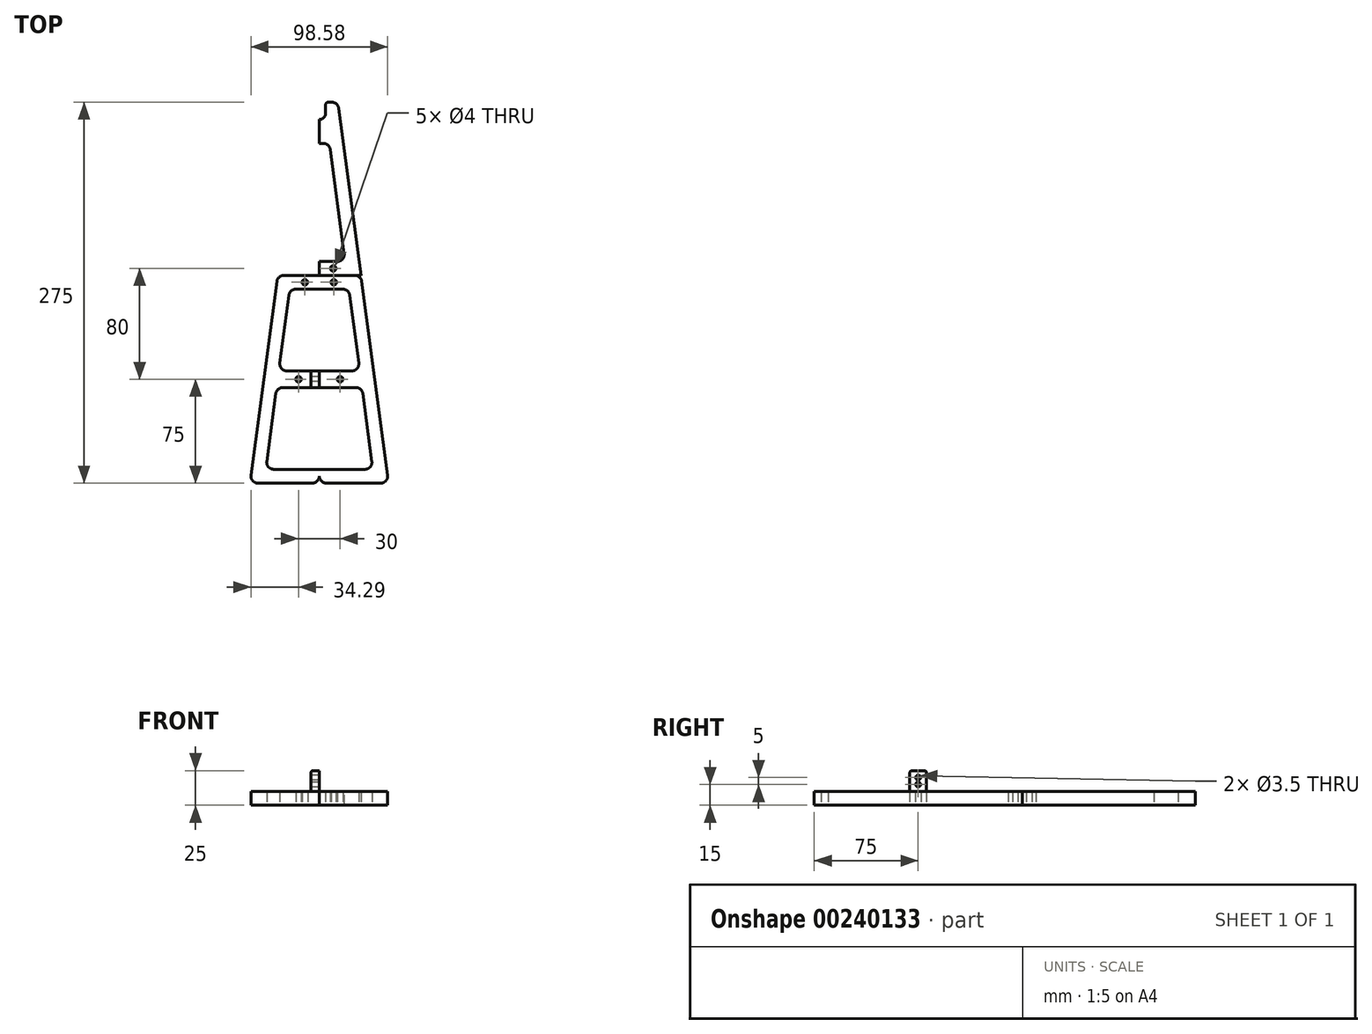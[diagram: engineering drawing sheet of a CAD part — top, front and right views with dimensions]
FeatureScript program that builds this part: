
annotation { "Feature Type Name" : "Feature", "Feature Type Description" : "" }
export const myFeature = defineFeature(function(context is Context, id is Id, definition is map)
    precondition{}
    {
        {
            var Q0;
            Q0=qCreatedBy(makeId("Top.planeOp"),FACE);
            var sketch = newSketch(context, id + "F0", { "sketchPlane" : qUnion([Q0])});
            skLineSegment(sketch, "E0.top", {"start": v(0, 75) * mm, "end": v(-30, 75) * mm});
            skPoint(sketch, "E0.middle", {"position": v(0, 0) * mm});
            skLineSegment(sketch, "E1", {"start": v(-30, 75) * mm, "end": v(-50, -75) * mm});
            skPoint(sketch, "E0.right.end.orphan", {"position": v(-50, 75) * mm});
            skPoint(sketch, "E0.left.end.orphan", {"position": v(50, 75) * mm});
            skLineSegment(sketch, "E2", {"start": v(0, 0) * mm, "end": v(0, 6) * mm});
            skLineSegment(sketch, "E3", {"start": v(-50, -75) * mm, "end": v(-40, -75) * mm});
            skLineSegment(sketch, "E4", {"start": v(-30, 75) * mm, "end": v(-20, 75) * mm});
            skLineSegment(sketch, "E5", {"start": v(0, 75) * mm, "end": v(0, 65) * mm});
            skLineSegment(sketch, "E6", {"start": v(0, 65) * mm, "end": v(-21.33, 65) * mm});
            skLineSegment(sketch, "E7", {"start": v(0, -75) * mm, "end": v(0, -65) * mm});
            skLineSegment(sketch, "E8", {"start": v(0, -65) * mm, "end": v(-38.67, -65) * mm});
            skLineSegment(sketch, "E9", {"start": v(0, 6) * mm, "end": v(-29.2, 6) * mm});
            skLineSegment(sketch, "E10", {"start": v(0, 0) * mm, "end": v(0, -6) * mm});
            skLineSegment(sketch, "E11", {"start": v(0, -6) * mm, "end": v(-30.8, -6) * mm});
            skLineSegment(sketch, "E12.trimOffspring", {"start": v(-30.8, -6) * mm, "end": v(-38.67, -65) * mm});
            skLineSegment(sketch, "E13", {"start": v(-21.33, 65) * mm, "end": v(-29.2, 6) * mm});
            skLineSegment(sketch, "E14.trimOffspring", {"start": v(0, -75) * mm, "end": v(-50, -75) * mm});
            skPoint(sketch, "E0.bottom.start.orphan", {"position": v(50, -75) * mm});
            skCircle(sketch, "E15", {"center": v(-15, 0) * mm, "radius": 2 * mm});
            skLineSegment(sketch, "E16", {"start": v(0, 65) * mm, "end": v(0, 70) * mm});
            skCircle(sketch, "E17", {"center": v(-10.41, 70) * mm, "radius": 2 * mm});
            skSolve(sketch);
        }
        {
            var Q0;
            Q0=qSketchRegion(id+"F0",true);
            extrude(context, id + "F1", {"entities" : qUnion([Q0]), "depth" : 10 * mm});
        }
        {
            var Q0;
            Q0=makeQuery(id+"F1.opExtrude","SWEPT_EDGE",EDGE,{"disambiguationData":[OSD([sQuery(id+"F0.wireOp",EDGE,"E6"),sQuery(id+"F0.wireOp",EDGE,"E13")])]});
            var Q1;
            Q1=makeQuery(id+"F1.opExtrude","SWEPT_EDGE",EDGE,{"disambiguationData":[OSD([sQuery(id+"F0.wireOp",EDGE,"E11"),sQuery(id+"F0.wireOp",EDGE,"E12.trimOffspring")])]});
            var Q2;
            Q2=makeQuery(id+"F1.opExtrude","SWEPT_EDGE",EDGE,{"disambiguationData":[OSD([sQuery(id+"F0.wireOp",EDGE,"E9"),sQuery(id+"F0.wireOp",EDGE,"E13")])]});
            var Q3;
            Q3=makeQuery(id+"F1.opExtrude","SWEPT_EDGE",EDGE,{"disambiguationData":[OSD([sQuery(id+"F0.wireOp",EDGE,"E8"),sQuery(id+"F0.wireOp",EDGE,"E12.trimOffspring")])]});
            var Q4;
            Q4=makeQuery(id+"F1.opExtrude","SWEPT_EDGE",EDGE,{"disambiguationData":[OSD([sQuery(id+"F0.wireOp",EDGE,"E1"),sQuery(id+"F0.wireOp",EDGE,"E14.trimOffspring")])]});
            fillet(context, id + "F2", {"entities" : qUnion([Q0, Q1, Q2, Q3, Q4]), "radius" : 5 * mm, "tangentPropagation" : true, "allowEdgeOverflow" : false});
        }
        {
            var Q0;
            Q0=makeQuery(id+"F1.opExtrude","SWEPT_BODY",BODY,{"disambiguationData":[OSD([sQuery(id+"F0.wireOp",EDGE,"E0.top"),sQuery(id+"F0.wireOp",EDGE,"E1"),sQuery(id+"F0.wireOp",EDGE,"E2"),sQuery(id+"F0.wireOp",EDGE,"E4"),sQuery(id+"F0.wireOp",EDGE,"E5"),sQuery(id+"F0.wireOp",EDGE,"E6"),sQuery(id+"F0.wireOp",EDGE,"E7"),sQuery(id+"F0.wireOp",EDGE,"E8"),sQuery(id+"F0.wireOp",EDGE,"E9"),sQuery(id+"F0.wireOp",EDGE,"E10"),sQuery(id+"F0.wireOp",EDGE,"E11"),sQuery(id+"F0.wireOp",EDGE,"E12.trimOffspring"),sQuery(id+"F0.wireOp",EDGE,"E13"),sQuery(id+"F0.wireOp",EDGE,"E14.trimOffspring"),sQuery(id+"F0.wireOp",EDGE,"E15"),sQuery(id+"F0.wireOp",EDGE,"E16"),sQuery(id+"F0.wireOp",EDGE,"E17")])]});
            var Q1;
            Q1=qCreatedBy(makeId("Right.planeOp"),FACE);
            mirror(context, id + "F3", {"operationType" : NewBodyOperationType.ADD, "entities" : qUnion([Q0]), "mirrorPlane" : qUnion([Q1])});
        }
        {
            var Q0;
            Q0=qCreatedBy(makeId("Top.planeOp"),FACE);
            var sketch = newSketch(context, id + "F4", { "sketchPlane" : qUnion([Q0])});
            skLineSegment(sketch, "E18", {"start": v(0, 0) * mm, "end": v(40, 0) * mm});
            skLineSegment(sketch, "E19", {"start": v(0, 75) * mm, "end": v(30, 75) * mm});
            skLineSegment(sketch, "E20", {"start": v(0, 75) * mm, "end": v(0, 85) * mm});
            skLineSegment(sketch, "E21", {"start": v(4.5, 200) * mm, "end": v(13.33, 200) * mm});
            skLineSegment(sketch, "E22", {"start": v(30, 75) * mm, "end": v(13.33, 200) * mm});
            skArc(sketch, "E23", {"start": v(0, 187.5) * mm, "mid": v(3.18, 188.82) * mm, "end": v(4.5, 192) * mm});
            skLineSegment(sketch, "E24", {"start": v(4.5, 200) * mm, "end": v(4.5, 192) * mm});
            skLineSegment(sketch, "E25", {"start": v(0, 75) * mm, "end": v(0, 80) * mm});
            skCircle(sketch, "E26", {"center": v(10, 80) * mm, "radius": 2 * mm});
            skLineSegment(sketch, "E27", {"start": v(0, 75) * mm, "end": v(10, 75) * mm});
            skLineSegment(sketch, "E28", {"start": v(10, 85) * mm, "end": v(18.67, 85) * mm});
            skLineSegment(sketch, "E29", {"start": v(18.67, 85) * mm, "end": v(10, 150) * mm});
            skLineSegment(sketch, "E30", {"start": v(10, 85) * mm, "end": v(0, 85) * mm});
            skLineSegment(sketch, "E31", {"start": v(18.67, 85) * mm, "end": v(7.31, 170.17) * mm});
            skLineSegment(sketch, "E32", {"start": v(7.31, 170.17) * mm, "end": v(0, 170.17) * mm});
            skLineSegment(sketch, "E33.trimOffspring", {"start": v(0, 170.17) * mm, "end": v(0, 187.5) * mm});
            skSolve(sketch);
        }
        {
            var Q0;
            Q0 = qSketchRegion(id + "F4", true);
            extrude(context, id + "F5", {"entities" : qUnion([Q0]), "depth" : 10 * mm});
        }
        {
            var Q0;
            Q0=makeQuery(id+"F5.opExtrude","SWEPT_BODY",BODY,{"disambiguationData":[OSD([sQuery(id+"F4.wireOp",EDGE,"E19"),sQuery(id+"F4.wireOp",EDGE,"E20"),sQuery(id+"F4.wireOp",EDGE,"E21"),sQuery(id+"F4.wireOp",EDGE,"E22"),sQuery(id+"F4.wireOp",EDGE,"E23"),sQuery(id+"F4.wireOp",EDGE,"E24"),sQuery(id+"F4.wireOp",EDGE,"E25"),sQuery(id+"F4.wireOp",EDGE,"E26"),sQuery(id+"F4.wireOp",EDGE,"E27"),sQuery(id+"F4.wireOp",EDGE,"E28"),sQuery(id+"F4.wireOp",EDGE,"E30"),sQuery(id+"F4.wireOp",EDGE,"E31"),sQuery(id+"F4.wireOp",EDGE,"E32"),sQuery(id+"F4.wireOp",EDGE,"E33.trimOffspring")])]});
            var Q1;
            Q1=qCreatedBy(makeId("Right.planeOp"),FACE);
            mirror(context, id + "F6", {"entities" : qUnion([Q0]), "mirrorPlane" : qUnion([Q1])});
        }
        {
            var Q0;
            Q0=makeQuery(id+"F6.opPattern","COPY",EDGE,{"derivedFrom":makeQuery(id+"F5.opExtrude","SWEPT_EDGE",EDGE,{"disambiguationData":[OSD([sQuery(id+"F4.wireOp",EDGE,"E31"),sQuery(id+"F4.wireOp",EDGE,"E32")])]}),"instanceName":"1"});
            var Q1;
            Q1=makeQuery(id+"F5.opExtrude","SWEPT_EDGE",EDGE,{"disambiguationData":[OSD([sQuery(id+"F4.wireOp",EDGE,"E31"),sQuery(id+"F4.wireOp",EDGE,"E32")])]});
            var Q2;
            Q2=makeQuery(id+"F6.opPattern","COPY",EDGE,{"derivedFrom":makeQuery(id+"F5.opExtrude","SWEPT_EDGE",EDGE,{"disambiguationData":[OSD([sQuery(id+"F4.wireOp",EDGE,"E28"),sQuery(id+"F4.wireOp",EDGE,"E31")])]}),"instanceName":"1"});
            var Q3;
            Q3=makeQuery(id+"F5.opExtrude","SWEPT_EDGE",EDGE,{"disambiguationData":[OSD([sQuery(id+"F4.wireOp",EDGE,"E28"),sQuery(id+"F4.wireOp",EDGE,"E31")])]});
            var Q4;
            Q4=makeQuery(id+"F6.opPattern","COPY",EDGE,{"derivedFrom":makeQuery(id+"F5.opExtrude","SWEPT_EDGE",EDGE,{"disambiguationData":[OSD([sQuery(id+"F4.wireOp",EDGE,"E21"),sQuery(id+"F4.wireOp",EDGE,"E22")])]}),"instanceName":"1"});
            var Q5;
            Q5=makeQuery(id+"F5.opExtrude","SWEPT_EDGE",EDGE,{"disambiguationData":[OSD([sQuery(id+"F4.wireOp",EDGE,"E21"),sQuery(id+"F4.wireOp",EDGE,"E22")])]});
            fillet(context, id + "F7", {"entities" : qUnion([Q0, Q1, Q2, Q3, Q4, Q5]), "radius" : 5 * mm, "tangentPropagation" : true, "allowEdgeOverflow" : false});
        }
        {
            var Q0;
            Q0=makeQuery(id+"F5.opExtrude","SWEPT_EDGE",EDGE,{"disambiguationData":[OSD([sQuery(id+"F4.wireOp",EDGE,"E21"),sQuery(id+"F4.wireOp",EDGE,"E24")])]});
            var Q1;
            Q1=makeQuery(id+"F6.opPattern","COPY",EDGE,{"derivedFrom":makeQuery(id+"F5.opExtrude","SWEPT_EDGE",EDGE,{"disambiguationData":[OSD([sQuery(id+"F4.wireOp",EDGE,"E21"),sQuery(id+"F4.wireOp",EDGE,"E24")])]}),"instanceName":"1"});
            fillet(context, id + "F8", {"entities" : qUnion([Q0, Q1]), "radius" : 2 * mm, "tangentPropagation" : true, "allowEdgeOverflow" : false});
        }
        {
            var Q0;
            Q0=qCreatedBy(makeId("Top.planeOp"),FACE);
            var sketch = newSketch(context, id + "F9", { "sketchPlane" : qUnion([Q0])});
            skLineSegment(sketch, "E34", {"start": v(0, 0) * mm, "end": v(0, 6) * mm});
            skLineSegment(sketch, "E35", {"start": v(0, 6) * mm, "end": v(-6, 6) * mm});
            skLineSegment(sketch, "E36", {"start": v(-6, 6) * mm, "end": v(-6, -6) * mm});
            skLineSegment(sketch, "E37", {"start": v(-6, -6) * mm, "end": v(0, -6) * mm});
            skLineSegment(sketch, "E38", {"start": v(0, -6) * mm, "end": v(0, 0) * mm});
            skSolve(sketch);
        }
        {
            var Q0;
            Q0 = qSketchRegion(id + "F9", true);
            extrude(context, id + "F10", {"entities" : qUnion([Q0]), "operationType" : NewBodyOperationType.ADD, "depth" : 25 * mm});
        }
        {
            var Q0;
            Q0=makeQuery(id+"F10.opExtrude","SWEPT_EDGE",EDGE,{"disambiguationData":[OSD([sQuery(id+"F9.wireOp",EDGE,"E36"),sQuery(id+"F9.wireOp",EDGE,"E37")])]});
            var Q1;
            Q1=makeQuery(id+"F10.opExtrude","CAP_EDGE",EDGE,{"disambiguationData":[OSD([sQuery(id+"F9.wireOp",EDGE,"E36")])],"isStart":false});
            var Q2;
            Q2=makeQuery(id+"F10.opExtrude","CAP_EDGE",EDGE,{"disambiguationData":[OSD([sQuery(id+"F9.wireOp",EDGE,"E37")])],"isStart":false});
            var Q3;
            Q3=makeQuery(id+"F10.opExtrude","SWEPT_EDGE",EDGE,{"disambiguationData":[OSD([sQuery(id+"F9.wireOp",EDGE,"E35"),sQuery(id+"F9.wireOp",EDGE,"E36")])]});
            var Q4;
            Q4=makeQuery(id+"F10.opExtrude","CAP_EDGE",EDGE,{"disambiguationData":[OSD([sQuery(id+"F9.wireOp",EDGE,"E35")])],"isStart":false});
            fillet(context, id + "F11", {"entities" : qUnion([Q0, Q1, Q2, Q3, Q4]), "radius" : 1.5 * mm, "tangentPropagation" : true, "allowEdgeOverflow" : false});
        }
        {
            var Q0;
            Q0=qCreatedBy(makeId("Right.planeOp"),FACE);
            var sketch = newSketch(context, id + "F12", { "sketchPlane" : qUnion([Q0])});
            skCircle(sketch, "E39", {"center": v(0, 20) * mm, "radius": 1.75 * mm});
            skCircle(sketch, "E40", {"center": v(0, 15) * mm, "radius": 1.75 * mm});
            skSolve(sketch);
        }
        {
            var Q0;
            Q0 = qSketchRegion(id + "F12", true);
            extrude(context, id + "F13", {"entities" : qUnion([Q0]), "endBound" : BoundingType.SYMMETRIC, "depth" : 25 * mm});
        }
        {
            var Q0;
            Q0=makeQuery(id+"F13.opExtrude","SWEPT_BODY",BODY,{"disambiguationData":[OSD([sQuery(id+"F12.wireOp",EDGE,"E40")])]});
            var Q1;
            Q1=makeQuery(id+"F13.opExtrude","SWEPT_BODY",BODY,{"disambiguationData":[OSD([sQuery(id+"F12.wireOp",EDGE,"E39")])]});
            var Q2;
            Q2=makeQuery(id+"F1.opExtrude","SWEPT_BODY",BODY,{"disambiguationData":[OSD([sQuery(id+"F0.wireOp",EDGE,"E0.top"),sQuery(id+"F0.wireOp",EDGE,"E1"),sQuery(id+"F0.wireOp",EDGE,"E2"),sQuery(id+"F0.wireOp",EDGE,"E4"),sQuery(id+"F0.wireOp",EDGE,"E5"),sQuery(id+"F0.wireOp",EDGE,"E6"),sQuery(id+"F0.wireOp",EDGE,"E7"),sQuery(id+"F0.wireOp",EDGE,"E8"),sQuery(id+"F0.wireOp",EDGE,"E9"),sQuery(id+"F0.wireOp",EDGE,"E10"),sQuery(id+"F0.wireOp",EDGE,"E11"),sQuery(id+"F0.wireOp",EDGE,"E12.trimOffspring"),sQuery(id+"F0.wireOp",EDGE,"E13"),sQuery(id+"F0.wireOp",EDGE,"E14.trimOffspring"),sQuery(id+"F0.wireOp",EDGE,"E15"),sQuery(id+"F0.wireOp",EDGE,"E16"),sQuery(id+"F0.wireOp",EDGE,"E17")])]});
            booleanBodies(context, id + "F14", {"operationType" : BooleanOperationType.SUBTRACTION, "tools" : qUnion([Q0, Q1]), "targets" : qUnion([Q2])});
        }
        {
            var Q0;
            Q0=qCreatedBy(makeId("Top.planeOp"),FACE);
            var sketch = newSketch(context, id + "F15", { "sketchPlane" : qUnion([Q0])});
            skLineSegment(sketch, "E41.bottom", {"start": v(15, 65) * mm, "end": v(-15, 65) * mm});
            skLineSegment(sketch, "E41.top", {"start": v(15, 85) * mm, "end": v(-15, 85) * mm});
            skLineSegment(sketch, "E41.left", {"start": v(15, 65) * mm, "end": v(15, 85) * mm});
            skLineSegment(sketch, "E41.right", {"start": v(-15, 65) * mm, "end": v(-15, 85) * mm});
            skPoint(sketch, "E41.middle", {"position": v(0, 75) * mm});
            skLineSegment(sketch, "E42", {"start": v(0, 75) * mm, "end": v(0, 85) * mm});
            skLineSegment(sketch, "E43", {"start": v(0, 85) * mm, "end": v(0, 65) * mm});
            skLineSegment(sketch, "E44", {"start": v(0, 65) * mm, "end": v(-6, 65) * mm});
            skLineSegment(sketch, "E45", {"start": v(-6, 65) * mm, "end": v(-6, 85) * mm});
            skLineSegment(sketch, "E46", {"start": v(-6, 85) * mm, "end": v(0, 85) * mm});
            skSolve(sketch);
        }
        {
            var Q0;
            Q0 = qSketchRegion(id + "F15", true);
            extrude(context, id + "F16", {"entities" : qUnion([Q0]), "depth" : 10 * mm});
        }
        {
            var Q0;
            Q0=qCreatedBy(makeId("Top.planeOp"),FACE);
            var sketch = newSketch(context, id + "F17", { "sketchPlane" : qUnion([Q0])});
            skLineSegment(sketch, "E47", {"start": v(0, 65) * mm, "end": v(0, 85) * mm});
            skLineSegment(sketch, "E48", {"start": v(0, 85) * mm, "end": v(-6, 85) * mm});
            skLineSegment(sketch, "E49", {"start": v(-6, 85) * mm, "end": v(-6, 65) * mm});
            skLineSegment(sketch, "E50", {"start": v(-6, 65) * mm, "end": v(0, 65) * mm});
            skSolve(sketch);
        }
        {
            var Q0;
            Q0 = qSketchRegion(id + "F17", true);
            extrude(context, id + "F18", {"entities" : qUnion([Q0]), "depth" : 25 * mm});
        }
        {
            var Q0;
            Q0=makeQuery(id+"F16.opExtrude","SWEPT_BODY",BODY,{"disambiguationData":[OSD([sQuery(id+"F15.wireOp",EDGE,"E41.bottom"),sQuery(id+"F15.wireOp",EDGE,"E41.top"),sQuery(id+"F15.wireOp",EDGE,"E41.left"),sQuery(id+"F15.wireOp",EDGE,"E41.right"),sQuery(id+"F15.wireOp",EDGE,"E44"),sQuery(id+"F15.wireOp",EDGE,"E46")])]});
            var Q1;
            Q1=makeQuery(id+"F18.opExtrude","SWEPT_BODY",BODY,{"disambiguationData":[OSD([sQuery(id+"F17.wireOp",EDGE,"E47"),sQuery(id+"F17.wireOp",EDGE,"E48"),sQuery(id+"F17.wireOp",EDGE,"E49"),sQuery(id+"F17.wireOp",EDGE,"E50")])]});
            booleanBodies(context, id + "F19", {"operationType" : BooleanOperationType.UNION, "tools" : qUnion([Q0, Q1])});
        }
        {
            var Q0;
            Q0=makeQuery(id+"F16.opExtrude","SWEPT_BODY",BODY,{"disambiguationData":[OSD([sQuery(id+"F15.wireOp",EDGE,"E41.bottom"),sQuery(id+"F15.wireOp",EDGE,"E41.top"),sQuery(id+"F15.wireOp",EDGE,"E41.left"),sQuery(id+"F15.wireOp",EDGE,"E41.right"),sQuery(id+"F15.wireOp",EDGE,"E44"),sQuery(id+"F15.wireOp",EDGE,"E46")])]});
            transform(context, id + "F20", {"entities" : qUnion([Q0]), "transformType" : TransformType.TRANSLATION_3D, "dx" : 0 * mm, "dy" : 0 * mm, "dz" : 10 * mm, "makeCopy" : false});
        }
        {
            var Q0;
            Q0=qCreatedBy(makeId("Top.planeOp"),FACE);
            var sketch = newSketch(context, id + "F21", { "sketchPlane" : qUnion([Q0])});
            skCircle(sketch, "E51", {"center": v(-10, 80) * mm, "radius": 2 * mm});
            skCircle(sketch, "E52", {"center": v(10, 80) * mm, "radius": 2 * mm});
            skCircle(sketch, "E53", {"center": v(-10.4, 70) * mm, "radius": 2 * mm});
            skCircle(sketch, "E54", {"center": v(10.4, 70) * mm, "radius": 2 * mm});
            skSolve(sketch);
        }
        {
            var Q0;
            Q0 = qSketchRegion(id + "F21", true);
            extrude(context, id + "F22", {"entities" : qUnion([Q0]), "depth" : 30 * mm});
        }
        {
            var Q0;
            Q0=makeQuery(id+"F22.opExtrude","SWEPT_BODY",BODY,{"disambiguationData":[OSD([sQuery(id+"F21.wireOp",EDGE,"E54")])]});
            var Q1;
            Q1=makeQuery(id+"F22.opExtrude","SWEPT_BODY",BODY,{"disambiguationData":[OSD([sQuery(id+"F21.wireOp",EDGE,"E53")])]});
            var Q2;
            Q2=makeQuery(id+"F22.opExtrude","SWEPT_BODY",BODY,{"disambiguationData":[OSD([sQuery(id+"F21.wireOp",EDGE,"E52")])]});
            var Q3;
            Q3=makeQuery(id+"F22.opExtrude","SWEPT_BODY",BODY,{"disambiguationData":[OSD([sQuery(id+"F21.wireOp",EDGE,"E51")])]});
            var Q4;
            Q4=makeQuery(id+"F16.opExtrude","SWEPT_BODY",BODY,{"disambiguationData":[OSD([sQuery(id+"F15.wireOp",EDGE,"E41.bottom"),sQuery(id+"F15.wireOp",EDGE,"E41.top"),sQuery(id+"F15.wireOp",EDGE,"E41.left"),sQuery(id+"F15.wireOp",EDGE,"E41.right"),sQuery(id+"F15.wireOp",EDGE,"E44"),sQuery(id+"F15.wireOp",EDGE,"E46")])]});
            booleanBodies(context, id + "F23", {"operationType" : BooleanOperationType.SUBTRACTION, "tools" : qUnion([Q0, Q1, Q2, Q3]), "targets" : qUnion([Q4])});
        }
        {
            var Q0;
            Q0=qCreatedBy(makeId("Right.planeOp"),FACE);
            var sketch = newSketch(context, id + "F24", { "sketchPlane" : qUnion([Q0])});
            skCircle(sketch, "E55", {"center": v(80, 27.23) * mm, "radius": 2 * mm});
            skCircle(sketch, "E56", {"center": v(70, 27.23) * mm, "radius": 2 * mm});
            skSolve(sketch);
        }
        {
            var Q0;
            Q0 = qSketchRegion(id + "F24", true);
            extrude(context, id + "F25", {"entities" : qUnion([Q0]), "endBound" : BoundingType.SYMMETRIC, "depth" : 25 * mm});
        }
        {
            var Q0;
            Q0=makeQuery(id+"F25.opExtrude","SWEPT_BODY",BODY,{"disambiguationData":[OSD([sQuery(id+"F24.wireOp",EDGE,"E56")])]});
            var Q1;
            Q1=makeQuery(id+"F25.opExtrude","SWEPT_BODY",BODY,{"disambiguationData":[OSD([sQuery(id+"F24.wireOp",EDGE,"E55")])]});
            var Q2;
            Q2=makeQuery(id+"F16.opExtrude","SWEPT_BODY",BODY,{"disambiguationData":[OSD([sQuery(id+"F15.wireOp",EDGE,"E41.bottom"),sQuery(id+"F15.wireOp",EDGE,"E41.top"),sQuery(id+"F15.wireOp",EDGE,"E41.left"),sQuery(id+"F15.wireOp",EDGE,"E41.right"),sQuery(id+"F15.wireOp",EDGE,"E44"),sQuery(id+"F15.wireOp",EDGE,"E46")])]});
            booleanBodies(context, id + "F26", {"operationType" : BooleanOperationType.SUBTRACTION, "tools" : qUnion([Q0, Q1]), "targets" : qUnion([Q2])});
        }
        {
            var Q0;
            Q0=makeQuery(id+"F18.opExtrude","SWEPT_EDGE",EDGE,{"disambiguationData":[OSD([sQuery(id+"F17.wireOp",EDGE,"E49"),sQuery(id+"F17.wireOp",EDGE,"E50")])]});
            var Q1;
            Q1=makeQuery(id+"F18.opExtrude","CAP_EDGE",EDGE,{"disambiguationData":[OSD([sQuery(id+"F17.wireOp",EDGE,"E50")])],"isStart":false});
            var Q2;
            {var subQ0=sQuery(id+"F15.wireOp",EDGE,"E44");var subQ1=sQuery(id+"F15.wireOp",EDGE,"E41.bottom");var subQ2=sQuery(id+"F15.wireOp",EDGE,"E41.right");Q2=makeQuery(id+"F19.opBoolean","SPLIT",EDGE,{"disambiguationData":[TD([makeQuery(id+"F16.opExtrude","SWEPT_FACE",FACE,{"disambiguationData":[OSD([subQ2])]})])],"derivedFrom":makeQuery(id+"F16.opExtrude","CAP_EDGE",EDGE,{"disambiguationData":[OSD([subQ1,subQ0])],"isStart":false})});}
            var Q3;
            Q3=makeQuery(id+"F16.opExtrude","SWEPT_EDGE",EDGE,{"disambiguationData":[OSD([sQuery(id+"F15.wireOp",EDGE,"E41.bottom"),sQuery(id+"F15.wireOp",EDGE,"E41.right")])]});
            var Q4;
            {var subQ0=sQuery(id+"F15.wireOp",EDGE,"E41.left");var subQ1=sQuery(id+"F15.wireOp",EDGE,"E44");var subQ2=sQuery(id+"F15.wireOp",EDGE,"E41.bottom");Q4=makeQuery(id+"F19.opBoolean","SPLIT",EDGE,{"disambiguationData":[TD([makeQuery(id+"F16.opExtrude","SWEPT_FACE",FACE,{"disambiguationData":[OSD([subQ0])]})])],"derivedFrom":makeQuery(id+"F16.opExtrude","CAP_EDGE",EDGE,{"disambiguationData":[OSD([subQ2,subQ1])],"isStart":false})});}
            var Q5;
            Q5=makeQuery(id+"F16.opExtrude","SWEPT_EDGE",EDGE,{"disambiguationData":[OSD([sQuery(id+"F15.wireOp",EDGE,"E41.bottom"),sQuery(id+"F15.wireOp",EDGE,"E41.left")])]});
            var Q6;
            Q6=makeQuery(id+"F16.opExtrude","CAP_EDGE",EDGE,{"disambiguationData":[OSD([sQuery(id+"F15.wireOp",EDGE,"E41.left")])],"isStart":false});
            var Q7;
            Q7=makeQuery(id+"F16.opExtrude","CAP_EDGE",EDGE,{"disambiguationData":[OSD([sQuery(id+"F15.wireOp",EDGE,"E41.right")])],"isStart":false});
            var Q8;
            Q8=makeQuery(id+"F18.opExtrude","CAP_EDGE",EDGE,{"disambiguationData":[OSD([sQuery(id+"F17.wireOp",EDGE,"E49")])],"isStart":false});
            var Q9;
            {var subQ0=sQuery(id+"F15.wireOp",EDGE,"E41.right");var subQ1=sQuery(id+"F15.wireOp",EDGE,"E46");var subQ2=sQuery(id+"F15.wireOp",EDGE,"E41.top");Q9=makeQuery(id+"F19.opBoolean","SPLIT",EDGE,{"disambiguationData":[TD([makeQuery(id+"F16.opExtrude","SWEPT_FACE",FACE,{"disambiguationData":[OSD([subQ0])]})])],"derivedFrom":makeQuery(id+"F16.opExtrude","CAP_EDGE",EDGE,{"disambiguationData":[OSD([subQ2,subQ1])],"isStart":false})});}
            var Q10;
            Q10=makeQuery(id+"F16.opExtrude","SWEPT_EDGE",EDGE,{"disambiguationData":[OSD([sQuery(id+"F15.wireOp",EDGE,"E41.top"),sQuery(id+"F15.wireOp",EDGE,"E41.right")])]});
            var Q11;
            Q11=makeQuery(id+"F18.opExtrude","SWEPT_EDGE",EDGE,{"disambiguationData":[OSD([sQuery(id+"F17.wireOp",EDGE,"E48"),sQuery(id+"F17.wireOp",EDGE,"E49")])]});
            var Q12;
            Q12=makeQuery(id+"F18.opExtrude","CAP_EDGE",EDGE,{"disambiguationData":[OSD([sQuery(id+"F17.wireOp",EDGE,"E48")])],"isStart":false});
            var Q13;
            {var subQ0=sQuery(id+"F15.wireOp",EDGE,"E41.left");var subQ1=sQuery(id+"F15.wireOp",EDGE,"E46");var subQ2=sQuery(id+"F15.wireOp",EDGE,"E41.top");Q13=makeQuery(id+"F19.opBoolean","SPLIT",EDGE,{"disambiguationData":[TD([makeQuery(id+"F16.opExtrude","SWEPT_FACE",FACE,{"disambiguationData":[OSD([subQ0])]})])],"derivedFrom":makeQuery(id+"F16.opExtrude","CAP_EDGE",EDGE,{"disambiguationData":[OSD([subQ2,subQ1])],"isStart":false})});}
            var Q14;
            Q14=makeQuery(id+"F16.opExtrude","SWEPT_EDGE",EDGE,{"disambiguationData":[OSD([sQuery(id+"F15.wireOp",EDGE,"E41.top"),sQuery(id+"F15.wireOp",EDGE,"E41.left")])]});
            fillet(context, id + "F27", {"entities" : qUnion([Q0, Q1, Q2, Q3, Q4, Q5, Q6, Q7, Q8, Q9, Q10, Q11, Q12, Q13, Q14]), "radius" : 2 * mm, "tangentPropagation" : true, "allowEdgeOverflow" : false});
        }
        {
            var Q0;
            Q0=qCreatedBy(makeId("Right.planeOp"),FACE);
            var sketch = newSketch(context, id + "F28", { "sketchPlane" : qUnion([Q0])});
            skLineSegment(sketch, "E57", {"start": v(0, 0) * mm, "end": v(0, 10) * mm});
            skLineSegment(sketch, "E58", {"start": v(0, 10) * mm, "end": v(6, 10) * mm});
            skLineSegment(sketch, "E59", {"start": v(6, 10) * mm, "end": v(6, 25) * mm});
            skLineSegment(sketch, "E60", {"start": v(-6, 25) * mm, "end": v(-6, 10) * mm});
            skLineSegment(sketch, "E61", {"start": v(-6, 10) * mm, "end": v(0, 10) * mm});
            skLineSegment(sketch, "E62", {"start": v(75, 10) * mm, "end": v(75, 20) * mm});
            skLineSegment(sketch, "E63", {"start": v(75, 20) * mm, "end": v(85, 20) * mm});
            skLineSegment(sketch, "E64", {"start": v(85, 20) * mm, "end": v(85, 35) * mm});
            skLineSegment(sketch, "E65", {"start": v(65, 35) * mm, "end": v(65, 20) * mm});
            skLineSegment(sketch, "E66", {"start": v(65, 20) * mm, "end": v(75, 20) * mm});
            skLineSegment(sketch, "E67", {"start": v(-6, 10) * mm, "end": v(-6, 25) * mm});
            skLineSegment(sketch, "E68", {"start": v(75, 120) * mm, "end": v(85, 120) * mm});
            skLineSegment(sketch, "E69", {"start": v(85, 35) * mm, "end": v(85, 120) * mm});
            skLineSegment(sketch, "E70", {"start": v(85, 120) * mm, "end": v(75, 120) * mm});
            skLineSegment(sketch, "E71", {"start": v(6, 25) * mm, "end": v(65, 35) * mm});
            skLineSegment(sketch, "E72", {"start": v(-6, 25) * mm, "end": v(75, 120) * mm});
            skLineSegment(sketch, "E73", {"start": v(23.92, 44.68) * mm, "end": v(75, 104.59) * mm});
            skLineSegment(sketch, "E74", {"start": v(23.92, 44.68) * mm, "end": v(17.44, 37.08) * mm});
            skLineSegment(sketch, "E75", {"start": v(75, 45) * mm, "end": v(64.16, 45) * mm});
            skLineSegment(sketch, "E76", {"start": v(51.92, 42.93) * mm, "end": v(17.44, 37.08) * mm});
            skLineSegment(sketch, "E77", {"start": v(51.92, 42.93) * mm, "end": v(64.16, 45) * mm});
            skPoint(sketch, "E78.orphan", {"position": v(75, 35) * mm});
            skPoint(sketch, "E79.start.orphan", {"position": v(75, 110) * mm});
            skLineSegment(sketch, "E80", {"start": v(75, 104.59) * mm, "end": v(75, 45) * mm});
            skCircle(sketch, "E81", {"center": v(80, 110) * mm, "radius": 2 * mm});
            skCircle(sketch, "E82", {"center": v(80, 95) * mm, "radius": 2 * mm});
            skPoint(sketch, "E83.end.orphan", {"position": v(80, 120) * mm});
            skSolve(sketch);
        }
        {
            var Q0;
            Q0 = qSketchRegion(id + "F28", true);
            extrude(context, id + "F29", {"entities" : qUnion([Q0]), "depth" : 8 * mm});
        }
        {
            var Q0;
            Q0=makeQuery(id+"F29.opExtrude","SWEPT_EDGE",EDGE,{"disambiguationData":[OSD([sQuery(id+"F28.wireOp",EDGE,"E73"),sQuery(id+"F28.wireOp",EDGE,"E80")])]});
            var Q1;
            Q1=makeQuery(id+"F29.opExtrude","SWEPT_EDGE",EDGE,{"disambiguationData":[OSD([sQuery(id+"F28.wireOp",EDGE,"E75"),sQuery(id+"F28.wireOp",EDGE,"E80")])]});
            var Q2;
            Q2=makeQuery(id+"F29.opExtrude","SWEPT_EDGE",EDGE,{"disambiguationData":[OSD([sQuery(id+"F28.wireOp",EDGE,"E74"),sQuery(id+"F28.wireOp",EDGE,"E76")])]});
            var Q3;
            Q3=makeQuery(id+"F29.opExtrude","SWEPT_EDGE",EDGE,{"disambiguationData":[OSD([sQuery(id+"F28.wireOp",EDGE,"E65"),sQuery(id+"F28.wireOp",EDGE,"E71")])]});
            var Q4;
            Q4=makeQuery(id+"F29.opExtrude","SWEPT_EDGE",EDGE,{"disambiguationData":[OSD([sQuery(id+"F28.wireOp",EDGE,"E59"),sQuery(id+"F28.wireOp",EDGE,"E71")])]});
            var Q5;
            Q5=makeQuery(id+"F29.opExtrude","SWEPT_EDGE",EDGE,{"disambiguationData":[OSD([sQuery(id+"F28.wireOp",EDGE,"E67"),sQuery(id+"F28.wireOp",EDGE,"E72")])]});
            fillet(context, id + "F30", {"entities" : qUnion([Q0, Q1, Q2, Q3, Q4, Q5]), "radius" : 2 * mm, "tangentPropagation" : true, "allowEdgeOverflow" : false});
        }
        {
            var Q0;
            Q0=makeQuery(id+"F29.opExtrude","CAP_EDGE",EDGE,{"disambiguationData":[OSD([sQuery(id+"F28.wireOp",EDGE,"E73"),sQuery(id+"F28.wireOp",EDGE,"E74")])],"isStart":false});
            var Q1;
            Q1=makeQuery(id+"F29.opExtrude","CAP_EDGE",EDGE,{"disambiguationData":[OSD([sQuery(id+"F28.wireOp",EDGE,"E72")])],"isStart":false});
            var Q2;
            Q2=makeQuery(id+"F29.opExtrude","CAP_EDGE",EDGE,{"disambiguationData":[OSD([sQuery(id+"F28.wireOp",EDGE,"E71")])],"isStart":false});
            var Q3;
            Q3=makeQuery(id+"F29.opExtrude","CAP_EDGE",EDGE,{"disambiguationData":[OSD([sQuery(id+"F28.wireOp",EDGE,"E64"),sQuery(id+"F28.wireOp",EDGE,"E69")])],"isStart":false});
            fillet(context, id + "F31", {"entities" : qUnion([Q0, Q1, Q2, Q3]), "radius" : 2 * mm, "tangentPropagation" : true, "allowEdgeOverflow" : false});
        }
        {
            var Q0;
            Q0=qCreatedBy(makeId("Right.planeOp"),FACE);
            var sketch = newSketch(context, id + "F32", { "sketchPlane" : qUnion([Q0])});
            skCircle(sketch, "E84", {"center": v(0, 20) * mm, "radius": 1.75 * mm});
            skCircle(sketch, "E85", {"center": v(0, 15) * mm, "radius": 1.75 * mm});
            skCircle(sketch, "E86", {"center": v(70, 27.25) * mm, "radius": 2 * mm});
            skCircle(sketch, "E87", {"center": v(80, 27.25) * mm, "radius": 2 * mm});
            skSolve(sketch);
        }
        {
            var Q0;
            Q0 = qSketchRegion(id + "F32", true);
            extrude(context, id + "F33", {"entities" : qUnion([Q0]), "depth" : 25 * mm});
        }
        {
            var Q0;
            Q0=makeQuery(id+"F33.opExtrude","SWEPT_BODY",BODY,{"disambiguationData":[OSD([sQuery(id+"F32.wireOp",EDGE,"E87")])]});
            var Q1;
            Q1=makeQuery(id+"F33.opExtrude","SWEPT_BODY",BODY,{"disambiguationData":[OSD([sQuery(id+"F32.wireOp",EDGE,"E86")])]});
            var Q2;
            Q2=makeQuery(id+"F33.opExtrude","SWEPT_BODY",BODY,{"disambiguationData":[OSD([sQuery(id+"F32.wireOp",EDGE,"E85")])]});
            var Q3;
            Q3=makeQuery(id+"F33.opExtrude","SWEPT_BODY",BODY,{"disambiguationData":[OSD([sQuery(id+"F32.wireOp",EDGE,"E84")])]});
            var Q4;
            Q4=makeQuery(id+"F29.opExtrude","SWEPT_BODY",BODY,{"disambiguationData":[OSD([sQuery(id+"F28.wireOp",EDGE,"E59"),sQuery(id+"F28.wireOp",EDGE,"E61"),sQuery(id+"F28.wireOp",EDGE,"E58"),sQuery(id+"F28.wireOp",EDGE,"E63"),sQuery(id+"F28.wireOp",EDGE,"E64"),sQuery(id+"F28.wireOp",EDGE,"E65"),sQuery(id+"F28.wireOp",EDGE,"E66"),sQuery(id+"F28.wireOp",EDGE,"E67"),sQuery(id+"F28.wireOp",EDGE,"E69"),sQuery(id+"F28.wireOp",EDGE,"E70"),sQuery(id+"F28.wireOp",EDGE,"E71"),sQuery(id+"F28.wireOp",EDGE,"E72"),sQuery(id+"F28.wireOp",EDGE,"E73"),sQuery(id+"F28.wireOp",EDGE,"E74"),sQuery(id+"F28.wireOp",EDGE,"E75"),sQuery(id+"F28.wireOp",EDGE,"E76"),sQuery(id+"F28.wireOp",EDGE,"E77"),sQuery(id+"F28.wireOp",EDGE,"E80"),sQuery(id+"F28.wireOp",EDGE,"E81"),sQuery(id+"F28.wireOp",EDGE,"E82")])]});
            booleanBodies(context, id + "F34", {"operationType" : BooleanOperationType.SUBTRACTION, "tools" : qUnion([Q0, Q1, Q2, Q3]), "targets" : qUnion([Q4])});
        }
        {
            var Q0;
            Q0=makeQuery(id+"F29.opExtrude","SWEPT_BODY",BODY,{"disambiguationData":[OSD([sQuery(id+"F28.wireOp",EDGE,"E59"),sQuery(id+"F28.wireOp",EDGE,"E61"),sQuery(id+"F28.wireOp",EDGE,"E58"),sQuery(id+"F28.wireOp",EDGE,"E63"),sQuery(id+"F28.wireOp",EDGE,"E64"),sQuery(id+"F28.wireOp",EDGE,"E65"),sQuery(id+"F28.wireOp",EDGE,"E66"),sQuery(id+"F28.wireOp",EDGE,"E67"),sQuery(id+"F28.wireOp",EDGE,"E69"),sQuery(id+"F28.wireOp",EDGE,"E70"),sQuery(id+"F28.wireOp",EDGE,"E71"),sQuery(id+"F28.wireOp",EDGE,"E72"),sQuery(id+"F28.wireOp",EDGE,"E73"),sQuery(id+"F28.wireOp",EDGE,"E74"),sQuery(id+"F28.wireOp",EDGE,"E75"),sQuery(id+"F28.wireOp",EDGE,"E76"),sQuery(id+"F28.wireOp",EDGE,"E77"),sQuery(id+"F28.wireOp",EDGE,"E80"),sQuery(id+"F28.wireOp",EDGE,"E81"),sQuery(id+"F28.wireOp",EDGE,"E82")])]});
            deleteBodies(context, id + "F35", {"entities" : qUnion([Q0])});
        }
        {
            var Q0;
            Q0=makeQuery(id+"F16.opExtrude","SWEPT_BODY",BODY,{"disambiguationData":[OSD([sQuery(id+"F15.wireOp",EDGE,"E41.bottom"),sQuery(id+"F15.wireOp",EDGE,"E41.top"),sQuery(id+"F15.wireOp",EDGE,"E41.left"),sQuery(id+"F15.wireOp",EDGE,"E41.right"),sQuery(id+"F15.wireOp",EDGE,"E44"),sQuery(id+"F15.wireOp",EDGE,"E46")])]});
            deleteBodies(context, id + "F36", {"entities" : qUnion([Q0])});
        }
        {
            var Q0;
            Q0=makeQuery(id+"F6.opPattern","COPY",BODY,{"derivedFrom":makeQuery(id+"F5.opExtrude","SWEPT_BODY",BODY,{"disambiguationData":[OSD([sQuery(id+"F4.wireOp",EDGE,"E19"),sQuery(id+"F4.wireOp",EDGE,"E20"),sQuery(id+"F4.wireOp",EDGE,"E21"),sQuery(id+"F4.wireOp",EDGE,"E22"),sQuery(id+"F4.wireOp",EDGE,"E23"),sQuery(id+"F4.wireOp",EDGE,"E24"),sQuery(id+"F4.wireOp",EDGE,"E25"),sQuery(id+"F4.wireOp",EDGE,"E26"),sQuery(id+"F4.wireOp",EDGE,"E27"),sQuery(id+"F4.wireOp",EDGE,"E28"),sQuery(id+"F4.wireOp",EDGE,"E30"),sQuery(id+"F4.wireOp",EDGE,"E31"),sQuery(id+"F4.wireOp",EDGE,"E32"),sQuery(id+"F4.wireOp",EDGE,"E33.trimOffspring")])]}),"instanceName":"1"});
            deleteBodies(context, id + "F37", {"entities" : qUnion([Q0])});
        }
    });
